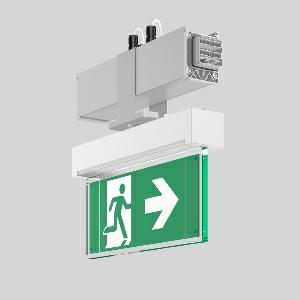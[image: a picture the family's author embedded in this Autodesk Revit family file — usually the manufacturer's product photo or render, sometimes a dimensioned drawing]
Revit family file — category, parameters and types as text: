
# Revit family: linedo_module_rz_9503rz_760_400_023_4eb6
name_source: partatom
category: Lighting Fixtures
units: mm (PartAtom-declared; Revit-internal decimal feet)

## family parameters
Cut with Voids When Loaded = No
Host = Face
Light Source = No
Part Type = Normal
Room Calculation Point = No
Round Connector Dimension = Use Diameter
Shared = No

## types (1)
- LINEDO Module RZ
    Apparent Load = 0 VA
    Default Elevation = 1800 mm
    Description = LINEDO, silver, on/off
Continuous line luminaire, L 336 B 62 H 308, CBS, Stromkreis
    Height = 308 mm
    Lamp = 0 x
    Length = 336 mm
    Luminous efficacy = 0 lm/W
    Manufacturer = RZB
    ModVariant = No
    Model = 9503RZ.760.400.023
    Mounting Place = Ceiling
    Mounting Type = Surface mounted
    Number of Poles = 1
    OnlyDefault = Yes
    Power Factor = 1
    Product Name = LINEDO Module RZ
    Product group = Continuous line luminaire system Linedo IP 54
    ProductGroupID = 314
    Protection Class = Protection class I
    Protection Degree = IP 54
    RLX_Detail_Level = 1
    RLX_Emergency_Light_Flux = 0 lm
    RLX_Emergency_Type = 0
    RLX_Emergency_Type_DB = No
    RlxData = <blob elided: 34809 chars, md5=59d38f41>
    Standby Power = 0 W
    System Light Flux = 0 lm
    System Power = 0 W
    Type Comments = Product without accessories
    Type Image = 9503rz.760.434.023.jpg
    URL = http://relux.com
    VarID = ---
    Voltage = 0 V
    Weight = 0.00 kg
    Width = 62 mm  [stored 0.203412 ft]

note: [stored X ft] marks values corroborated as IEEE doubles in the binary element streams (Revit-internal decimal feet)

## geometry (parser evidence)
native form markers: Blend x4, Sweep x11
no freeform markers — native parametric forms only
